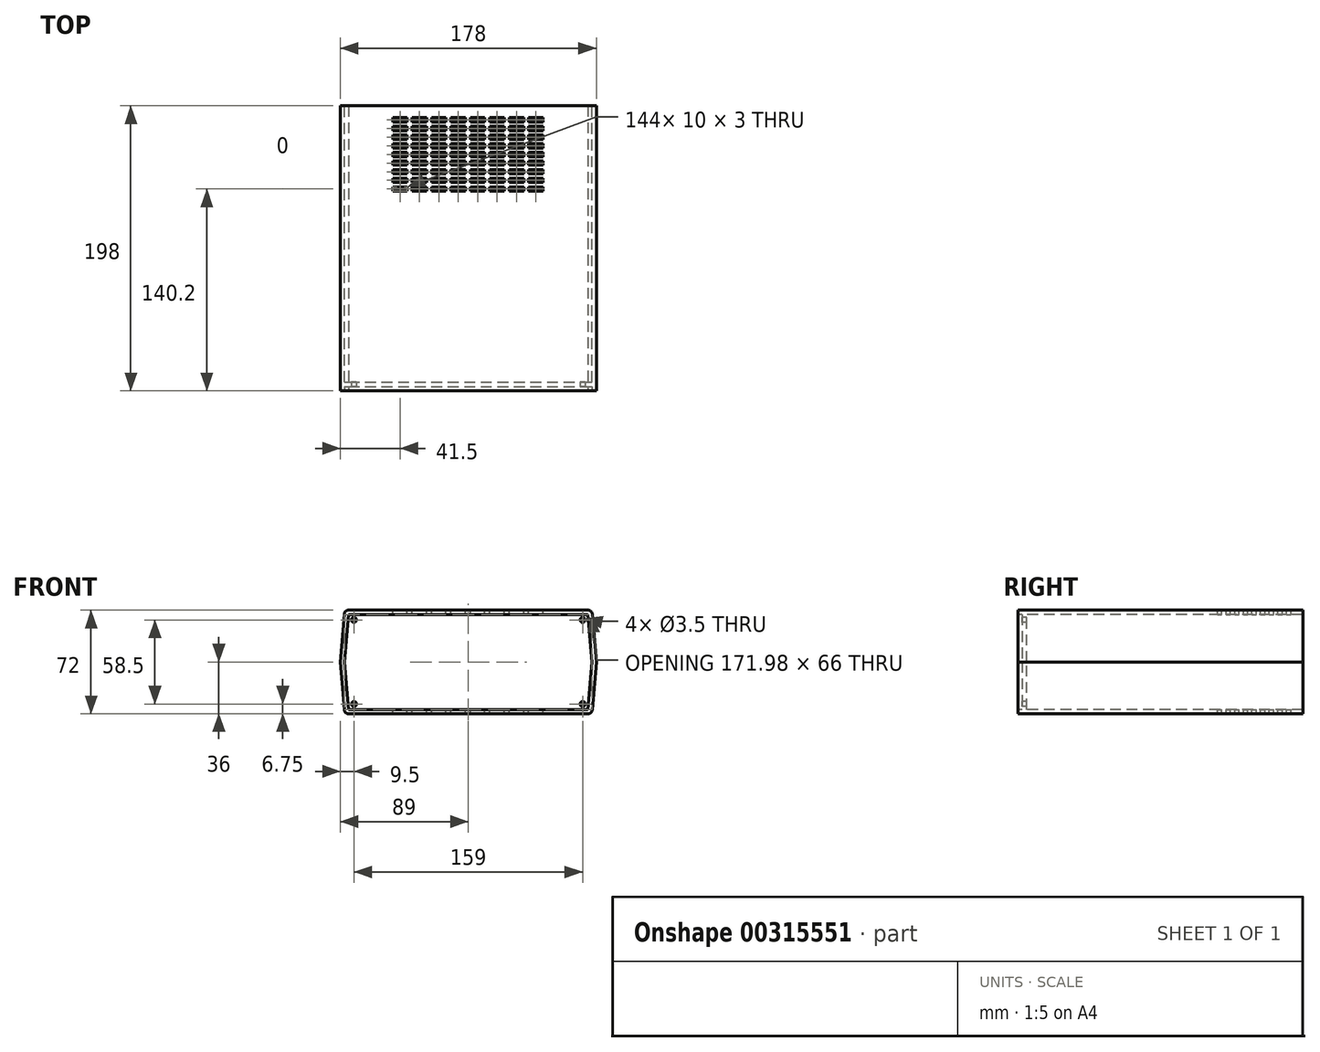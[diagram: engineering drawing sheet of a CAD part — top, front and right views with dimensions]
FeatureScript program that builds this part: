
annotation { "Feature Type Name" : "Feature", "Feature Type Description" : "" }
export const myFeature = defineFeature(function(context is Context, id is Id, definition is map)
    precondition{}
    {
        {
            var Q0;
            Q0=qCreatedBy(makeId("Front.planeOp"),FACE);
            var sketch = newSketch(context, id + "F0", { "sketchPlane" : qUnion([Q0])});
            skLineSegment(sketch, "E0", {"start": v(-89, 0) * mm, "end": v(-86, 36) * mm});
            skLineSegment(sketch, "E1", {"start": v(-86, 36) * mm, "end": v(86, 36) * mm});
            skLineSegment(sketch, "E2", {"start": v(86, 36) * mm, "end": v(89, 0) * mm});
            skLineSegment(sketch, "E3", {"start": v(-89, 0) * mm, "end": v(89, 0) * mm, "construction": true});
            skLineSegment(sketch, "E4", {"start": v(0, 0) * mm, "end": v(0, 36) * mm, "construction": true});
            skLineSegment(sketch, "E5.MirrorCS", {"start": v(86, -36) * mm, "end": v(89, 0) * mm});
            skLineSegment(sketch, "E6.MirrorCS", {"start": v(-89, 0) * mm, "end": v(-86, -36) * mm});
            skLineSegment(sketch, "E7.MirrorCS", {"start": v(-86, -36) * mm, "end": v(86, -36) * mm});
            skSolve(sketch);
        }
        {
            var Q0;
            Q0 = qSketchRegion(id + "F0", true);
            extrude(context, id + "F1", {"entities" : qUnion([Q0]), "depth" : 198 * mm});
        }
        {
            var Q0;
            Q0=makeQuery(id+"F1.opExtrude","SWEPT_EDGE",EDGE,{"disambiguationData":[OSD([sQuery(id+"F0.wireOp",EDGE,"E1"),sQuery(id+"F0.wireOp",EDGE,"E2")])]});
            var Q1;
            Q1=makeQuery(id+"F1.opExtrude","SWEPT_EDGE",EDGE,{"disambiguationData":[OSD([sQuery(id+"F0.wireOp",EDGE,"E0"),sQuery(id+"F0.wireOp",EDGE,"E1")])]});
            var Q2;
            Q2=makeQuery(id+"F1.opExtrude","SWEPT_EDGE",EDGE,{"disambiguationData":[OSD([sQuery(id+"F0.wireOp",EDGE,"E6.MirrorCS"),sQuery(id+"F0.wireOp",EDGE,"E7.MirrorCS")])]});
            var Q3;
            Q3=makeQuery(id+"F1.opExtrude","SWEPT_EDGE",EDGE,{"disambiguationData":[OSD([sQuery(id+"F0.wireOp",EDGE,"E5.MirrorCS"),sQuery(id+"F0.wireOp",EDGE,"E7.MirrorCS")])]});
            fillet(context, id + "F2", {"entities" : qUnion([Q0, Q1, Q2, Q3]), "radius" : 3 * mm, "tangentPropagation" : true, "allowEdgeOverflow" : false});
        }
        {
            var Q0;
            Q0=makeQuery(id+"F1.opExtrude","CAP_FACE",FACE,{"disambiguationData":[OSD([sQuery(id+"F0.wireOp",EDGE,"E0"),sQuery(id+"F0.wireOp",EDGE,"E1"),sQuery(id+"F0.wireOp",EDGE,"E2"),sQuery(id+"F0.wireOp",EDGE,"E5.MirrorCS"),sQuery(id+"F0.wireOp",EDGE,"E6.MirrorCS"),sQuery(id+"F0.wireOp",EDGE,"E7.MirrorCS")])],"isStart":false});
            var sketch = newSketch(context, id + "F3", { "sketchPlane" : qUnion([Q0])});
            skLineSegment(sketch, "E8.0", {"start": v(-83.24, 36) * mm, "end": v(83.24, 36) * mm, "construction": true});
            skArc(sketch, "E9.0", {"start": v(86.23, 33.25) * mm, "mid": v(85.27, 35.2) * mm, "end": v(83.24, 36) * mm, "construction": true});
            skLineSegment(sketch, "E9.1", {"start": v(86.23, 33.25) * mm, "end": v(89, 0) * mm, "construction": true});
            skLineSegment(sketch, "E10.0", {"start": v(86.23, -33.25) * mm, "end": v(89, 0) * mm, "construction": true});
            skArc(sketch, "E10.1", {"start": v(83.24, -36) * mm, "mid": v(85.27, -35.2) * mm, "end": v(86.23, -33.25) * mm, "construction": true});
            skLineSegment(sketch, "E10.2", {"start": v(-83.24, -36) * mm, "end": v(83.24, -36) * mm, "construction": true});
            skArc(sketch, "E11.0", {"start": v(-86.23, -33.25) * mm, "mid": v(-85.27, -35.2) * mm, "end": v(-83.24, -36) * mm, "construction": true});
            skLineSegment(sketch, "E11.1", {"start": v(-89, 0) * mm, "end": v(-86.23, -33.25) * mm, "construction": true});
            skLineSegment(sketch, "E12.0", {"start": v(-89, 0) * mm, "end": v(-86.23, 33.25) * mm, "construction": true});
            skArc(sketch, "E12.1", {"start": v(-83.24, 36) * mm, "mid": v(-85.27, 35.2) * mm, "end": v(-86.23, 33.25) * mm, "construction": true});
            skLineSegment(sketch, "E13.0", {"start": v(-85.99, 0) * mm, "end": v(-83.24, -33) * mm});
            skLineSegment(sketch, "E13.1", {"start": v(83.24, -33) * mm, "end": v(85.99, 0) * mm});
            skLineSegment(sketch, "E13.2", {"start": v(83.24, 33) * mm, "end": v(85.99, 0) * mm});
            skLineSegment(sketch, "E13.3", {"start": v(-83.24, -33) * mm, "end": v(83.24, -33) * mm});
            skLineSegment(sketch, "E13.4", {"start": v(-83.24, 33) * mm, "end": v(83.24, 33) * mm});
            skLineSegment(sketch, "E13.5", {"start": v(-85.99, 0) * mm, "end": v(-83.24, 33) * mm});
            skSolve(sketch);
        }
        {
            var Q0;
            Q0=makeQuery(id+"F3.imprint","IMPRINT",FACE,{"disambiguationData":[TD([[makeQuery(id+"F3.imprint","IMPRINT",EDGE,{"derivedFrom":sQuery(id+"F3.wireOp",EDGE,"E13.0")}),1.0]])]});
            extrude(context, id + "F4", {"entities" : qUnion([Q0]), "operationType" : NewBodyOperationType.REMOVE, "oppositeDirection" : true, "depth" : 3 * mm});
        }
        {
            var Q0;
            Q0=makeQuery(id+"F1.opExtrude","CAP_FACE",FACE,{"disambiguationData":[OSD([sQuery(id+"F0.wireOp",EDGE,"E0"),sQuery(id+"F0.wireOp",EDGE,"E1"),sQuery(id+"F0.wireOp",EDGE,"E2"),sQuery(id+"F0.wireOp",EDGE,"E5.MirrorCS"),sQuery(id+"F0.wireOp",EDGE,"E6.MirrorCS"),sQuery(id+"F0.wireOp",EDGE,"E7.MirrorCS")])],"isStart":true});
            shell(context, id + "F5", {"entities" : qUnion([Q0]), "thickness" : 3 * mm});
        }
        {
            var Q0;
            Q0=makeQuery(id+"F4.boolean.opBoolean","COPY",FACE,{"derivedFrom":makeQuery(id+"F4.opExtrude","CAP_FACE",FACE,{"disambiguationData":[OSD([sQuery(id+"F3.wireOp",EDGE,"E13.0"),sQuery(id+"F3.wireOp",EDGE,"E13.1"),sQuery(id+"F3.wireOp",EDGE,"E13.2"),sQuery(id+"F3.wireOp",EDGE,"E13.3"),sQuery(id+"F3.wireOp",EDGE,"E13.4"),sQuery(id+"F3.wireOp",EDGE,"E13.5")])],"isStart":false})});
            var sketch = newSketch(context, id + "F6", { "sketchPlane" : qUnion([Q0])});
            skCircle(sketch, "E14", {"center": v(-79.5, 29.25) * mm, "radius": 1.75 * mm});
            skCircle(sketch, "E15", {"center": v(79.5, 29.25) * mm, "radius": 1.75 * mm});
            skLineSegment(sketch, "E16", {"start": v(0, 0) * mm, "end": v(85.99, 0) * mm, "construction": true});
            skLineSegment(sketch, "E17", {"start": v(0, 0) * mm, "end": v(0, 33) * mm, "construction": true});
            skCircle(sketch, "E18.MirrorC", {"center": v(79.5, -29.25) * mm, "radius": 1.75 * mm});
            skCircle(sketch, "E19.MirrorC", {"center": v(-79.5, -29.25) * mm, "radius": 1.75 * mm});
            skSolve(sketch);
        }
        {
            var Q0;
            Q0 = qSketchRegion(id + "F6", true);
            extrude(context, id + "F7", {"entities" : qUnion([Q0]), "operationType" : NewBodyOperationType.REMOVE, "oppositeDirection" : true, "depth" : 25 * mm});
        }
        {
            var Q0;
            Q0=makeQuery(id+"F1.opExtrude","SWEPT_FACE",FACE,{"disambiguationData":[OSD([sQuery(id+"F0.wireOp",EDGE,"E1")])]});
            var sketch = newSketch(context, id + "F8", { "sketchPlane" : qUnion([Q0])});
            skLineSegment(sketch, "E20.bottom", {"start": v(52.5, -7) * mm, "end": v(-52.5, -7) * mm, "construction": true});
            skLineSegment(sketch, "E20.top", {"start": v(52.5, -59.3) * mm, "end": v(-52.5, -59.3) * mm, "construction": true});
            skLineSegment(sketch, "E20.left", {"start": v(52.5, -7) * mm, "end": v(52.5, -59.3) * mm, "construction": true});
            skLineSegment(sketch, "E20.right", {"start": v(-52.5, -7) * mm, "end": v(-52.5, -59.3) * mm, "construction": true});
            skPoint(sketch, "E20.middle", {"position": v(0, -33.15) * mm});
            skLineSegment(sketch, "E21.bottom", {"start": v(-52.5, -59.3) * mm, "end": v(-42.5, -59.3) * mm});
            skLineSegment(sketch, "E21.top", {"start": v(-52.5, -56.3) * mm, "end": v(-42.5, -56.3) * mm});
            skLineSegment(sketch, "E21.left", {"start": v(-52.5, -59.3) * mm, "end": v(-52.5, -56.3) * mm});
            skLineSegment(sketch, "E21.right", {"start": v(-42.5, -59.3) * mm, "end": v(-42.5, -56.3) * mm});
            skLineSegment(sketch, "E22.0.1.0", {"start": v(-52.5, -50.3) * mm, "end": v(-42.5, -50.3) * mm});
            skLineSegment(sketch, "E22.0.1.1", {"start": v(-52.5, -53.3) * mm, "end": v(-42.5, -53.3) * mm});
            skLineSegment(sketch, "E22.0.1.2", {"start": v(-52.5, -53.3) * mm, "end": v(-52.5, -50.3) * mm});
            skLineSegment(sketch, "E22.0.1.3", {"start": v(-42.5, -53.3) * mm, "end": v(-42.5, -50.3) * mm});
            skLineSegment(sketch, "E22.0.2.0", {"start": v(-52.5, -44.3) * mm, "end": v(-42.5, -44.3) * mm});
            skLineSegment(sketch, "E22.0.2.1", {"start": v(-52.5, -47.3) * mm, "end": v(-42.5, -47.3) * mm});
            skLineSegment(sketch, "E22.0.2.2", {"start": v(-52.5, -47.3) * mm, "end": v(-52.5, -44.3) * mm});
            skLineSegment(sketch, "E22.0.2.3", {"start": v(-42.5, -47.3) * mm, "end": v(-42.5, -44.3) * mm});
            skLineSegment(sketch, "E22.0.3.0", {"start": v(-52.5, -38.3) * mm, "end": v(-42.5, -38.3) * mm});
            skLineSegment(sketch, "E22.0.3.1", {"start": v(-52.5, -41.3) * mm, "end": v(-42.5, -41.3) * mm});
            skLineSegment(sketch, "E22.0.3.2", {"start": v(-52.5, -41.3) * mm, "end": v(-52.5, -38.3) * mm});
            skLineSegment(sketch, "E22.0.3.3", {"start": v(-42.5, -41.3) * mm, "end": v(-42.5, -38.3) * mm});
            skLineSegment(sketch, "E22.0.4.0", {"start": v(-52.5, -32.3) * mm, "end": v(-42.5, -32.3) * mm});
            skLineSegment(sketch, "E22.0.4.1", {"start": v(-52.5, -35.3) * mm, "end": v(-42.5, -35.3) * mm});
            skLineSegment(sketch, "E22.0.4.2", {"start": v(-52.5, -35.3) * mm, "end": v(-52.5, -32.3) * mm});
            skLineSegment(sketch, "E22.0.4.3", {"start": v(-42.5, -35.3) * mm, "end": v(-42.5, -32.3) * mm});
            skLineSegment(sketch, "E22.0.5.0", {"start": v(-52.5, -26.3) * mm, "end": v(-42.5, -26.3) * mm});
            skLineSegment(sketch, "E22.0.5.1", {"start": v(-52.5, -29.3) * mm, "end": v(-42.5, -29.3) * mm});
            skLineSegment(sketch, "E22.0.5.2", {"start": v(-52.5, -29.3) * mm, "end": v(-52.5, -26.3) * mm});
            skLineSegment(sketch, "E22.0.5.3", {"start": v(-42.5, -29.3) * mm, "end": v(-42.5, -26.3) * mm});
            skLineSegment(sketch, "E22.0.6.0", {"start": v(-52.5, -20.3) * mm, "end": v(-42.5, -20.3) * mm});
            skLineSegment(sketch, "E22.0.6.1", {"start": v(-52.5, -23.3) * mm, "end": v(-42.5, -23.3) * mm});
            skLineSegment(sketch, "E22.0.6.2", {"start": v(-52.5, -23.3) * mm, "end": v(-52.5, -20.3) * mm});
            skLineSegment(sketch, "E22.0.6.3", {"start": v(-42.5, -23.3) * mm, "end": v(-42.5, -20.3) * mm});
            skLineSegment(sketch, "E22.0.7.0", {"start": v(-52.5, -14.3) * mm, "end": v(-42.5, -14.3) * mm});
            skLineSegment(sketch, "E22.0.7.1", {"start": v(-52.5, -17.3) * mm, "end": v(-42.5, -17.3) * mm});
            skLineSegment(sketch, "E22.0.7.2", {"start": v(-52.5, -17.3) * mm, "end": v(-52.5, -14.3) * mm});
            skLineSegment(sketch, "E22.0.7.3", {"start": v(-42.5, -17.3) * mm, "end": v(-42.5, -14.3) * mm});
            skLineSegment(sketch, "E22.0.8.0", {"start": v(-52.5, -8.3) * mm, "end": v(-42.5, -8.3) * mm});
            skLineSegment(sketch, "E22.0.8.1", {"start": v(-52.5, -11.3) * mm, "end": v(-42.5, -11.3) * mm});
            skLineSegment(sketch, "E22.0.8.2", {"start": v(-52.5, -11.3) * mm, "end": v(-52.5, -8.3) * mm});
            skLineSegment(sketch, "E22.0.8.3", {"start": v(-42.5, -11.3) * mm, "end": v(-42.5, -8.3) * mm});
            skLineSegment(sketch, "E22.1.0.0", {"start": v(-39, -56.3) * mm, "end": v(-29, -56.3) * mm});
            skLineSegment(sketch, "E22.1.0.1", {"start": v(-39, -59.3) * mm, "end": v(-29, -59.3) * mm});
            skLineSegment(sketch, "E22.1.0.2", {"start": v(-39, -59.3) * mm, "end": v(-39, -56.3) * mm});
            skLineSegment(sketch, "E22.1.0.3", {"start": v(-29, -59.3) * mm, "end": v(-29, -56.3) * mm});
            skLineSegment(sketch, "E22.1.1.0", {"start": v(-39, -50.3) * mm, "end": v(-29, -50.3) * mm});
            skLineSegment(sketch, "E22.1.1.1", {"start": v(-39, -53.3) * mm, "end": v(-29, -53.3) * mm});
            skLineSegment(sketch, "E22.1.1.2", {"start": v(-39, -53.3) * mm, "end": v(-39, -50.3) * mm});
            skLineSegment(sketch, "E22.1.1.3", {"start": v(-29, -53.3) * mm, "end": v(-29, -50.3) * mm});
            skLineSegment(sketch, "E22.1.2.0", {"start": v(-39, -44.3) * mm, "end": v(-29, -44.3) * mm});
            skLineSegment(sketch, "E22.1.2.1", {"start": v(-39, -47.3) * mm, "end": v(-29, -47.3) * mm});
            skLineSegment(sketch, "E22.1.2.2", {"start": v(-39, -47.3) * mm, "end": v(-39, -44.3) * mm});
            skLineSegment(sketch, "E22.1.2.3", {"start": v(-29, -47.3) * mm, "end": v(-29, -44.3) * mm});
            skLineSegment(sketch, "E22.1.3.0", {"start": v(-39, -38.3) * mm, "end": v(-29, -38.3) * mm});
            skLineSegment(sketch, "E22.1.3.1", {"start": v(-39, -41.3) * mm, "end": v(-29, -41.3) * mm});
            skLineSegment(sketch, "E22.1.3.2", {"start": v(-39, -41.3) * mm, "end": v(-39, -38.3) * mm});
            skLineSegment(sketch, "E22.1.3.3", {"start": v(-29, -41.3) * mm, "end": v(-29, -38.3) * mm});
            skLineSegment(sketch, "E22.1.4.0", {"start": v(-39, -32.3) * mm, "end": v(-29, -32.3) * mm});
            skLineSegment(sketch, "E22.1.4.1", {"start": v(-39, -35.3) * mm, "end": v(-29, -35.3) * mm});
            skLineSegment(sketch, "E22.1.4.2", {"start": v(-39, -35.3) * mm, "end": v(-39, -32.3) * mm});
            skLineSegment(sketch, "E22.1.4.3", {"start": v(-29, -35.3) * mm, "end": v(-29, -32.3) * mm});
            skLineSegment(sketch, "E22.1.5.0", {"start": v(-39, -26.3) * mm, "end": v(-29, -26.3) * mm});
            skLineSegment(sketch, "E22.1.5.1", {"start": v(-39, -29.3) * mm, "end": v(-29, -29.3) * mm});
            skLineSegment(sketch, "E22.1.5.2", {"start": v(-39, -29.3) * mm, "end": v(-39, -26.3) * mm});
            skLineSegment(sketch, "E22.1.5.3", {"start": v(-29, -29.3) * mm, "end": v(-29, -26.3) * mm});
            skLineSegment(sketch, "E22.1.6.0", {"start": v(-39, -20.3) * mm, "end": v(-29, -20.3) * mm});
            skLineSegment(sketch, "E22.1.6.1", {"start": v(-39, -23.3) * mm, "end": v(-29, -23.3) * mm});
            skLineSegment(sketch, "E22.1.6.2", {"start": v(-39, -23.3) * mm, "end": v(-39, -20.3) * mm});
            skLineSegment(sketch, "E22.1.6.3", {"start": v(-29, -23.3) * mm, "end": v(-29, -20.3) * mm});
            skLineSegment(sketch, "E22.1.7.0", {"start": v(-39, -14.3) * mm, "end": v(-29, -14.3) * mm});
            skLineSegment(sketch, "E22.1.7.1", {"start": v(-39, -17.3) * mm, "end": v(-29, -17.3) * mm});
            skLineSegment(sketch, "E22.1.7.2", {"start": v(-39, -17.3) * mm, "end": v(-39, -14.3) * mm});
            skLineSegment(sketch, "E22.1.7.3", {"start": v(-29, -17.3) * mm, "end": v(-29, -14.3) * mm});
            skLineSegment(sketch, "E22.1.8.0", {"start": v(-39, -8.3) * mm, "end": v(-29, -8.3) * mm});
            skLineSegment(sketch, "E22.1.8.1", {"start": v(-39, -11.3) * mm, "end": v(-29, -11.3) * mm});
            skLineSegment(sketch, "E22.1.8.2", {"start": v(-39, -11.3) * mm, "end": v(-39, -8.3) * mm});
            skLineSegment(sketch, "E22.1.8.3", {"start": v(-29, -11.3) * mm, "end": v(-29, -8.3) * mm});
            skLineSegment(sketch, "E22.2.0.0", {"start": v(-25.5, -56.3) * mm, "end": v(-15.5, -56.3) * mm});
            skLineSegment(sketch, "E22.2.0.1", {"start": v(-25.5, -59.3) * mm, "end": v(-15.5, -59.3) * mm});
            skLineSegment(sketch, "E22.2.0.2", {"start": v(-25.5, -59.3) * mm, "end": v(-25.5, -56.3) * mm});
            skLineSegment(sketch, "E22.2.0.3", {"start": v(-15.5, -59.3) * mm, "end": v(-15.5, -56.3) * mm});
            skLineSegment(sketch, "E22.2.1.0", {"start": v(-25.5, -50.3) * mm, "end": v(-15.5, -50.3) * mm});
            skLineSegment(sketch, "E22.2.1.1", {"start": v(-25.5, -53.3) * mm, "end": v(-15.5, -53.3) * mm});
            skLineSegment(sketch, "E22.2.1.2", {"start": v(-25.5, -53.3) * mm, "end": v(-25.5, -50.3) * mm});
            skLineSegment(sketch, "E22.2.1.3", {"start": v(-15.5, -53.3) * mm, "end": v(-15.5, -50.3) * mm});
            skLineSegment(sketch, "E22.2.2.0", {"start": v(-25.5, -44.3) * mm, "end": v(-15.5, -44.3) * mm});
            skLineSegment(sketch, "E22.2.2.1", {"start": v(-25.5, -47.3) * mm, "end": v(-15.5, -47.3) * mm});
            skLineSegment(sketch, "E22.2.2.2", {"start": v(-25.5, -47.3) * mm, "end": v(-25.5, -44.3) * mm});
            skLineSegment(sketch, "E22.2.2.3", {"start": v(-15.5, -47.3) * mm, "end": v(-15.5, -44.3) * mm});
            skLineSegment(sketch, "E22.2.3.0", {"start": v(-25.5, -38.3) * mm, "end": v(-15.5, -38.3) * mm});
            skLineSegment(sketch, "E22.2.3.1", {"start": v(-25.5, -41.3) * mm, "end": v(-15.5, -41.3) * mm});
            skLineSegment(sketch, "E22.2.3.2", {"start": v(-25.5, -41.3) * mm, "end": v(-25.5, -38.3) * mm});
            skLineSegment(sketch, "E22.2.3.3", {"start": v(-15.5, -41.3) * mm, "end": v(-15.5, -38.3) * mm});
            skLineSegment(sketch, "E22.2.4.0", {"start": v(-25.5, -32.3) * mm, "end": v(-15.5, -32.3) * mm});
            skLineSegment(sketch, "E22.2.4.1", {"start": v(-25.5, -35.3) * mm, "end": v(-15.5, -35.3) * mm});
            skLineSegment(sketch, "E22.2.4.2", {"start": v(-25.5, -35.3) * mm, "end": v(-25.5, -32.3) * mm});
            skLineSegment(sketch, "E22.2.4.3", {"start": v(-15.5, -35.3) * mm, "end": v(-15.5, -32.3) * mm});
            skLineSegment(sketch, "E22.2.5.0", {"start": v(-25.5, -26.3) * mm, "end": v(-15.5, -26.3) * mm});
            skLineSegment(sketch, "E22.2.5.1", {"start": v(-25.5, -29.3) * mm, "end": v(-15.5, -29.3) * mm});
            skLineSegment(sketch, "E22.2.5.2", {"start": v(-25.5, -29.3) * mm, "end": v(-25.5, -26.3) * mm});
            skLineSegment(sketch, "E22.2.5.3", {"start": v(-15.5, -29.3) * mm, "end": v(-15.5, -26.3) * mm});
            skLineSegment(sketch, "E22.2.6.0", {"start": v(-25.5, -20.3) * mm, "end": v(-15.5, -20.3) * mm});
            skLineSegment(sketch, "E22.2.6.1", {"start": v(-25.5, -23.3) * mm, "end": v(-15.5, -23.3) * mm});
            skLineSegment(sketch, "E22.2.6.2", {"start": v(-25.5, -23.3) * mm, "end": v(-25.5, -20.3) * mm});
            skLineSegment(sketch, "E22.2.6.3", {"start": v(-15.5, -23.3) * mm, "end": v(-15.5, -20.3) * mm});
            skLineSegment(sketch, "E22.2.7.0", {"start": v(-25.5, -14.3) * mm, "end": v(-15.5, -14.3) * mm});
            skLineSegment(sketch, "E22.2.7.1", {"start": v(-25.5, -17.3) * mm, "end": v(-15.5, -17.3) * mm});
            skLineSegment(sketch, "E22.2.7.2", {"start": v(-25.5, -17.3) * mm, "end": v(-25.5, -14.3) * mm});
            skLineSegment(sketch, "E22.2.7.3", {"start": v(-15.5, -17.3) * mm, "end": v(-15.5, -14.3) * mm});
            skLineSegment(sketch, "E22.2.8.0", {"start": v(-25.5, -8.3) * mm, "end": v(-15.5, -8.3) * mm});
            skLineSegment(sketch, "E22.2.8.1", {"start": v(-25.5, -11.3) * mm, "end": v(-15.5, -11.3) * mm});
            skLineSegment(sketch, "E22.2.8.2", {"start": v(-25.5, -11.3) * mm, "end": v(-25.5, -8.3) * mm});
            skLineSegment(sketch, "E22.2.8.3", {"start": v(-15.5, -11.3) * mm, "end": v(-15.5, -8.3) * mm});
            skLineSegment(sketch, "E22.3.0.0", {"start": v(-12, -56.3) * mm, "end": v(-2, -56.3) * mm});
            skLineSegment(sketch, "E22.3.0.1", {"start": v(-12, -59.3) * mm, "end": v(-2, -59.3) * mm});
            skLineSegment(sketch, "E22.3.0.2", {"start": v(-12, -59.3) * mm, "end": v(-12, -56.3) * mm});
            skLineSegment(sketch, "E22.3.0.3", {"start": v(-2, -59.3) * mm, "end": v(-2, -56.3) * mm});
            skLineSegment(sketch, "E22.3.1.0", {"start": v(-12, -50.3) * mm, "end": v(-2, -50.3) * mm});
            skLineSegment(sketch, "E22.3.1.1", {"start": v(-12, -53.3) * mm, "end": v(-2, -53.3) * mm});
            skLineSegment(sketch, "E22.3.1.2", {"start": v(-12, -53.3) * mm, "end": v(-12, -50.3) * mm});
            skLineSegment(sketch, "E22.3.1.3", {"start": v(-2, -53.3) * mm, "end": v(-2, -50.3) * mm});
            skLineSegment(sketch, "E22.3.2.0", {"start": v(-12, -44.3) * mm, "end": v(-2, -44.3) * mm});
            skLineSegment(sketch, "E22.3.2.1", {"start": v(-12, -47.3) * mm, "end": v(-2, -47.3) * mm});
            skLineSegment(sketch, "E22.3.2.2", {"start": v(-12, -47.3) * mm, "end": v(-12, -44.3) * mm});
            skLineSegment(sketch, "E22.3.2.3", {"start": v(-2, -47.3) * mm, "end": v(-2, -44.3) * mm});
            skLineSegment(sketch, "E22.3.3.0", {"start": v(-12, -38.3) * mm, "end": v(-2, -38.3) * mm});
            skLineSegment(sketch, "E22.3.3.1", {"start": v(-12, -41.3) * mm, "end": v(-2, -41.3) * mm});
            skLineSegment(sketch, "E22.3.3.2", {"start": v(-12, -41.3) * mm, "end": v(-12, -38.3) * mm});
            skLineSegment(sketch, "E22.3.3.3", {"start": v(-2, -41.3) * mm, "end": v(-2, -38.3) * mm});
            skLineSegment(sketch, "E22.3.4.0", {"start": v(-12, -32.3) * mm, "end": v(-2, -32.3) * mm});
            skLineSegment(sketch, "E22.3.4.1", {"start": v(-12, -35.3) * mm, "end": v(-2, -35.3) * mm});
            skLineSegment(sketch, "E22.3.4.2", {"start": v(-12, -35.3) * mm, "end": v(-12, -32.3) * mm});
            skLineSegment(sketch, "E22.3.4.3", {"start": v(-2, -35.3) * mm, "end": v(-2, -32.3) * mm});
            skLineSegment(sketch, "E22.3.5.0", {"start": v(-12, -26.3) * mm, "end": v(-2, -26.3) * mm});
            skLineSegment(sketch, "E22.3.5.1", {"start": v(-12, -29.3) * mm, "end": v(-2, -29.3) * mm});
            skLineSegment(sketch, "E22.3.5.2", {"start": v(-12, -29.3) * mm, "end": v(-12, -26.3) * mm});
            skLineSegment(sketch, "E22.3.5.3", {"start": v(-2, -29.3) * mm, "end": v(-2, -26.3) * mm});
            skLineSegment(sketch, "E22.3.6.0", {"start": v(-12, -20.3) * mm, "end": v(-2, -20.3) * mm});
            skLineSegment(sketch, "E22.3.6.1", {"start": v(-12, -23.3) * mm, "end": v(-2, -23.3) * mm});
            skLineSegment(sketch, "E22.3.6.2", {"start": v(-12, -23.3) * mm, "end": v(-12, -20.3) * mm});
            skLineSegment(sketch, "E22.3.6.3", {"start": v(-2, -23.3) * mm, "end": v(-2, -20.3) * mm});
            skLineSegment(sketch, "E22.3.7.0", {"start": v(-12, -14.3) * mm, "end": v(-2, -14.3) * mm});
            skLineSegment(sketch, "E22.3.7.1", {"start": v(-12, -17.3) * mm, "end": v(-2, -17.3) * mm});
            skLineSegment(sketch, "E22.3.7.2", {"start": v(-12, -17.3) * mm, "end": v(-12, -14.3) * mm});
            skLineSegment(sketch, "E22.3.7.3", {"start": v(-2, -17.3) * mm, "end": v(-2, -14.3) * mm});
            skLineSegment(sketch, "E22.3.8.0", {"start": v(-12, -8.3) * mm, "end": v(-2, -8.3) * mm});
            skLineSegment(sketch, "E22.3.8.1", {"start": v(-12, -11.3) * mm, "end": v(-2, -11.3) * mm});
            skLineSegment(sketch, "E22.3.8.2", {"start": v(-12, -11.3) * mm, "end": v(-12, -8.3) * mm});
            skLineSegment(sketch, "E22.3.8.3", {"start": v(-2, -11.3) * mm, "end": v(-2, -8.3) * mm});
            skLineSegment(sketch, "E22.4.0.0", {"start": v(1.5, -56.3) * mm, "end": v(11.5, -56.3) * mm});
            skLineSegment(sketch, "E22.4.0.1", {"start": v(1.5, -59.3) * mm, "end": v(11.5, -59.3) * mm});
            skLineSegment(sketch, "E22.4.0.2", {"start": v(1.5, -59.3) * mm, "end": v(1.5, -56.3) * mm});
            skLineSegment(sketch, "E22.4.0.3", {"start": v(11.5, -59.3) * mm, "end": v(11.5, -56.3) * mm});
            skLineSegment(sketch, "E22.4.1.0", {"start": v(1.5, -50.3) * mm, "end": v(11.5, -50.3) * mm});
            skLineSegment(sketch, "E22.4.1.1", {"start": v(1.5, -53.3) * mm, "end": v(11.5, -53.3) * mm});
            skLineSegment(sketch, "E22.4.1.2", {"start": v(1.5, -53.3) * mm, "end": v(1.5, -50.3) * mm});
            skLineSegment(sketch, "E22.4.1.3", {"start": v(11.5, -53.3) * mm, "end": v(11.5, -50.3) * mm});
            skLineSegment(sketch, "E22.4.2.0", {"start": v(1.5, -44.3) * mm, "end": v(11.5, -44.3) * mm});
            skLineSegment(sketch, "E22.4.2.1", {"start": v(1.5, -47.3) * mm, "end": v(11.5, -47.3) * mm});
            skLineSegment(sketch, "E22.4.2.2", {"start": v(1.5, -47.3) * mm, "end": v(1.5, -44.3) * mm});
            skLineSegment(sketch, "E22.4.2.3", {"start": v(11.5, -47.3) * mm, "end": v(11.5, -44.3) * mm});
            skLineSegment(sketch, "E22.4.3.0", {"start": v(1.5, -38.3) * mm, "end": v(11.5, -38.3) * mm});
            skLineSegment(sketch, "E22.4.3.1", {"start": v(1.5, -41.3) * mm, "end": v(11.5, -41.3) * mm});
            skLineSegment(sketch, "E22.4.3.2", {"start": v(1.5, -41.3) * mm, "end": v(1.5, -38.3) * mm});
            skLineSegment(sketch, "E22.4.3.3", {"start": v(11.5, -41.3) * mm, "end": v(11.5, -38.3) * mm});
            skLineSegment(sketch, "E22.4.4.0", {"start": v(1.5, -32.3) * mm, "end": v(11.5, -32.3) * mm});
            skLineSegment(sketch, "E22.4.4.1", {"start": v(1.5, -35.3) * mm, "end": v(11.5, -35.3) * mm});
            skLineSegment(sketch, "E22.4.4.2", {"start": v(1.5, -35.3) * mm, "end": v(1.5, -32.3) * mm});
            skLineSegment(sketch, "E22.4.4.3", {"start": v(11.5, -35.3) * mm, "end": v(11.5, -32.3) * mm});
            skLineSegment(sketch, "E22.4.5.0", {"start": v(1.5, -26.3) * mm, "end": v(11.5, -26.3) * mm});
            skLineSegment(sketch, "E22.4.5.1", {"start": v(1.5, -29.3) * mm, "end": v(11.5, -29.3) * mm});
            skLineSegment(sketch, "E22.4.5.2", {"start": v(1.5, -29.3) * mm, "end": v(1.5, -26.3) * mm});
            skLineSegment(sketch, "E22.4.5.3", {"start": v(11.5, -29.3) * mm, "end": v(11.5, -26.3) * mm});
            skLineSegment(sketch, "E22.4.6.0", {"start": v(1.5, -20.3) * mm, "end": v(11.5, -20.3) * mm});
            skLineSegment(sketch, "E22.4.6.1", {"start": v(1.5, -23.3) * mm, "end": v(11.5, -23.3) * mm});
            skLineSegment(sketch, "E22.4.6.2", {"start": v(1.5, -23.3) * mm, "end": v(1.5, -20.3) * mm});
            skLineSegment(sketch, "E22.4.6.3", {"start": v(11.5, -23.3) * mm, "end": v(11.5, -20.3) * mm});
            skLineSegment(sketch, "E22.4.7.0", {"start": v(1.5, -14.3) * mm, "end": v(11.5, -14.3) * mm});
            skLineSegment(sketch, "E22.4.7.1", {"start": v(1.5, -17.3) * mm, "end": v(11.5, -17.3) * mm});
            skLineSegment(sketch, "E22.4.7.2", {"start": v(1.5, -17.3) * mm, "end": v(1.5, -14.3) * mm});
            skLineSegment(sketch, "E22.4.7.3", {"start": v(11.5, -17.3) * mm, "end": v(11.5, -14.3) * mm});
            skLineSegment(sketch, "E22.4.8.0", {"start": v(1.5, -8.3) * mm, "end": v(11.5, -8.3) * mm});
            skLineSegment(sketch, "E22.4.8.1", {"start": v(1.5, -11.3) * mm, "end": v(11.5, -11.3) * mm});
            skLineSegment(sketch, "E22.4.8.2", {"start": v(1.5, -11.3) * mm, "end": v(1.5, -8.3) * mm});
            skLineSegment(sketch, "E22.4.8.3", {"start": v(11.5, -11.3) * mm, "end": v(11.5, -8.3) * mm});
            skLineSegment(sketch, "E22.5.0.0", {"start": v(15, -56.3) * mm, "end": v(25, -56.3) * mm});
            skLineSegment(sketch, "E22.5.0.1", {"start": v(15, -59.3) * mm, "end": v(25, -59.3) * mm});
            skLineSegment(sketch, "E22.5.0.2", {"start": v(15, -59.3) * mm, "end": v(15, -56.3) * mm});
            skLineSegment(sketch, "E22.5.0.3", {"start": v(25, -59.3) * mm, "end": v(25, -56.3) * mm});
            skLineSegment(sketch, "E22.5.1.0", {"start": v(15, -50.3) * mm, "end": v(25, -50.3) * mm});
            skLineSegment(sketch, "E22.5.1.1", {"start": v(15, -53.3) * mm, "end": v(25, -53.3) * mm});
            skLineSegment(sketch, "E22.5.1.2", {"start": v(15, -53.3) * mm, "end": v(15, -50.3) * mm});
            skLineSegment(sketch, "E22.5.1.3", {"start": v(25, -53.3) * mm, "end": v(25, -50.3) * mm});
            skLineSegment(sketch, "E22.5.2.0", {"start": v(15, -44.3) * mm, "end": v(25, -44.3) * mm});
            skLineSegment(sketch, "E22.5.2.1", {"start": v(15, -47.3) * mm, "end": v(25, -47.3) * mm});
            skLineSegment(sketch, "E22.5.2.2", {"start": v(15, -47.3) * mm, "end": v(15, -44.3) * mm});
            skLineSegment(sketch, "E22.5.2.3", {"start": v(25, -47.3) * mm, "end": v(25, -44.3) * mm});
            skLineSegment(sketch, "E22.5.3.0", {"start": v(15, -38.3) * mm, "end": v(25, -38.3) * mm});
            skLineSegment(sketch, "E22.5.3.1", {"start": v(15, -41.3) * mm, "end": v(25, -41.3) * mm});
            skLineSegment(sketch, "E22.5.3.2", {"start": v(15, -41.3) * mm, "end": v(15, -38.3) * mm});
            skLineSegment(sketch, "E22.5.3.3", {"start": v(25, -41.3) * mm, "end": v(25, -38.3) * mm});
            skLineSegment(sketch, "E22.5.4.0", {"start": v(15, -32.3) * mm, "end": v(25, -32.3) * mm});
            skLineSegment(sketch, "E22.5.4.1", {"start": v(15, -35.3) * mm, "end": v(25, -35.3) * mm});
            skLineSegment(sketch, "E22.5.4.2", {"start": v(15, -35.3) * mm, "end": v(15, -32.3) * mm});
            skLineSegment(sketch, "E22.5.4.3", {"start": v(25, -35.3) * mm, "end": v(25, -32.3) * mm});
            skLineSegment(sketch, "E22.5.5.0", {"start": v(15, -26.3) * mm, "end": v(25, -26.3) * mm});
            skLineSegment(sketch, "E22.5.5.1", {"start": v(15, -29.3) * mm, "end": v(25, -29.3) * mm});
            skLineSegment(sketch, "E22.5.5.2", {"start": v(15, -29.3) * mm, "end": v(15, -26.3) * mm});
            skLineSegment(sketch, "E22.5.5.3", {"start": v(25, -29.3) * mm, "end": v(25, -26.3) * mm});
            skLineSegment(sketch, "E22.5.6.0", {"start": v(15, -20.3) * mm, "end": v(25, -20.3) * mm});
            skLineSegment(sketch, "E22.5.6.1", {"start": v(15, -23.3) * mm, "end": v(25, -23.3) * mm});
            skLineSegment(sketch, "E22.5.6.2", {"start": v(15, -23.3) * mm, "end": v(15, -20.3) * mm});
            skLineSegment(sketch, "E22.5.6.3", {"start": v(25, -23.3) * mm, "end": v(25, -20.3) * mm});
            skLineSegment(sketch, "E22.5.7.0", {"start": v(15, -14.3) * mm, "end": v(25, -14.3) * mm});
            skLineSegment(sketch, "E22.5.7.1", {"start": v(15, -17.3) * mm, "end": v(25, -17.3) * mm});
            skLineSegment(sketch, "E22.5.7.2", {"start": v(15, -17.3) * mm, "end": v(15, -14.3) * mm});
            skLineSegment(sketch, "E22.5.7.3", {"start": v(25, -17.3) * mm, "end": v(25, -14.3) * mm});
            skLineSegment(sketch, "E22.5.8.0", {"start": v(15, -8.3) * mm, "end": v(25, -8.3) * mm});
            skLineSegment(sketch, "E22.5.8.1", {"start": v(15, -11.3) * mm, "end": v(25, -11.3) * mm});
            skLineSegment(sketch, "E22.5.8.2", {"start": v(15, -11.3) * mm, "end": v(15, -8.3) * mm});
            skLineSegment(sketch, "E22.5.8.3", {"start": v(25, -11.3) * mm, "end": v(25, -8.3) * mm});
            skLineSegment(sketch, "E22.6.0.0", {"start": v(28.5, -56.3) * mm, "end": v(38.5, -56.3) * mm});
            skLineSegment(sketch, "E22.6.0.1", {"start": v(28.5, -59.3) * mm, "end": v(38.5, -59.3) * mm});
            skLineSegment(sketch, "E22.6.0.2", {"start": v(28.5, -59.3) * mm, "end": v(28.5, -56.3) * mm});
            skLineSegment(sketch, "E22.6.0.3", {"start": v(38.5, -59.3) * mm, "end": v(38.5, -56.3) * mm});
            skLineSegment(sketch, "E22.6.1.0", {"start": v(28.5, -50.3) * mm, "end": v(38.5, -50.3) * mm});
            skLineSegment(sketch, "E22.6.1.1", {"start": v(28.5, -53.3) * mm, "end": v(38.5, -53.3) * mm});
            skLineSegment(sketch, "E22.6.1.2", {"start": v(28.5, -53.3) * mm, "end": v(28.5, -50.3) * mm});
            skLineSegment(sketch, "E22.6.1.3", {"start": v(38.5, -53.3) * mm, "end": v(38.5, -50.3) * mm});
            skLineSegment(sketch, "E22.6.2.0", {"start": v(28.5, -44.3) * mm, "end": v(38.5, -44.3) * mm});
            skLineSegment(sketch, "E22.6.2.1", {"start": v(28.5, -47.3) * mm, "end": v(38.5, -47.3) * mm});
            skLineSegment(sketch, "E22.6.2.2", {"start": v(28.5, -47.3) * mm, "end": v(28.5, -44.3) * mm});
            skLineSegment(sketch, "E22.6.2.3", {"start": v(38.5, -47.3) * mm, "end": v(38.5, -44.3) * mm});
            skLineSegment(sketch, "E22.6.3.0", {"start": v(28.5, -38.3) * mm, "end": v(38.5, -38.3) * mm});
            skLineSegment(sketch, "E22.6.3.1", {"start": v(28.5, -41.3) * mm, "end": v(38.5, -41.3) * mm});
            skLineSegment(sketch, "E22.6.3.2", {"start": v(28.5, -41.3) * mm, "end": v(28.5, -38.3) * mm});
            skLineSegment(sketch, "E22.6.3.3", {"start": v(38.5, -41.3) * mm, "end": v(38.5, -38.3) * mm});
            skLineSegment(sketch, "E22.6.4.0", {"start": v(28.5, -32.3) * mm, "end": v(38.5, -32.3) * mm});
            skLineSegment(sketch, "E22.6.4.1", {"start": v(28.5, -35.3) * mm, "end": v(38.5, -35.3) * mm});
            skLineSegment(sketch, "E22.6.4.2", {"start": v(28.5, -35.3) * mm, "end": v(28.5, -32.3) * mm});
            skLineSegment(sketch, "E22.6.4.3", {"start": v(38.5, -35.3) * mm, "end": v(38.5, -32.3) * mm});
            skLineSegment(sketch, "E22.6.5.0", {"start": v(28.5, -26.3) * mm, "end": v(38.5, -26.3) * mm});
            skLineSegment(sketch, "E22.6.5.1", {"start": v(28.5, -29.3) * mm, "end": v(38.5, -29.3) * mm});
            skLineSegment(sketch, "E22.6.5.2", {"start": v(28.5, -29.3) * mm, "end": v(28.5, -26.3) * mm});
            skLineSegment(sketch, "E22.6.5.3", {"start": v(38.5, -29.3) * mm, "end": v(38.5, -26.3) * mm});
            skLineSegment(sketch, "E22.6.6.0", {"start": v(28.5, -20.3) * mm, "end": v(38.5, -20.3) * mm});
            skLineSegment(sketch, "E22.6.6.1", {"start": v(28.5, -23.3) * mm, "end": v(38.5, -23.3) * mm});
            skLineSegment(sketch, "E22.6.6.2", {"start": v(28.5, -23.3) * mm, "end": v(28.5, -20.3) * mm});
            skLineSegment(sketch, "E22.6.6.3", {"start": v(38.5, -23.3) * mm, "end": v(38.5, -20.3) * mm});
            skLineSegment(sketch, "E22.6.7.0", {"start": v(28.5, -14.3) * mm, "end": v(38.5, -14.3) * mm});
            skLineSegment(sketch, "E22.6.7.1", {"start": v(28.5, -17.3) * mm, "end": v(38.5, -17.3) * mm});
            skLineSegment(sketch, "E22.6.7.2", {"start": v(28.5, -17.3) * mm, "end": v(28.5, -14.3) * mm});
            skLineSegment(sketch, "E22.6.7.3", {"start": v(38.5, -17.3) * mm, "end": v(38.5, -14.3) * mm});
            skLineSegment(sketch, "E22.6.8.0", {"start": v(28.5, -8.3) * mm, "end": v(38.5, -8.3) * mm});
            skLineSegment(sketch, "E22.6.8.1", {"start": v(28.5, -11.3) * mm, "end": v(38.5, -11.3) * mm});
            skLineSegment(sketch, "E22.6.8.2", {"start": v(28.5, -11.3) * mm, "end": v(28.5, -8.3) * mm});
            skLineSegment(sketch, "E22.6.8.3", {"start": v(38.5, -11.3) * mm, "end": v(38.5, -8.3) * mm});
            skLineSegment(sketch, "E22.7.0.0", {"start": v(42, -56.3) * mm, "end": v(52, -56.3) * mm});
            skLineSegment(sketch, "E22.7.0.1", {"start": v(42, -59.3) * mm, "end": v(52, -59.3) * mm});
            skLineSegment(sketch, "E22.7.0.2", {"start": v(42, -59.3) * mm, "end": v(42, -56.3) * mm});
            skLineSegment(sketch, "E22.7.0.3", {"start": v(52, -59.3) * mm, "end": v(52, -56.3) * mm});
            skLineSegment(sketch, "E22.7.1.0", {"start": v(42, -50.3) * mm, "end": v(52, -50.3) * mm});
            skLineSegment(sketch, "E22.7.1.1", {"start": v(42, -53.3) * mm, "end": v(52, -53.3) * mm});
            skLineSegment(sketch, "E22.7.1.2", {"start": v(42, -53.3) * mm, "end": v(42, -50.3) * mm});
            skLineSegment(sketch, "E22.7.1.3", {"start": v(52, -53.3) * mm, "end": v(52, -50.3) * mm});
            skLineSegment(sketch, "E22.7.2.0", {"start": v(42, -44.3) * mm, "end": v(52, -44.3) * mm});
            skLineSegment(sketch, "E22.7.2.1", {"start": v(42, -47.3) * mm, "end": v(52, -47.3) * mm});
            skLineSegment(sketch, "E22.7.2.2", {"start": v(42, -47.3) * mm, "end": v(42, -44.3) * mm});
            skLineSegment(sketch, "E22.7.2.3", {"start": v(52, -47.3) * mm, "end": v(52, -44.3) * mm});
            skLineSegment(sketch, "E22.7.3.0", {"start": v(42, -38.3) * mm, "end": v(52, -38.3) * mm});
            skLineSegment(sketch, "E22.7.3.1", {"start": v(42, -41.3) * mm, "end": v(52, -41.3) * mm});
            skLineSegment(sketch, "E22.7.3.2", {"start": v(42, -41.3) * mm, "end": v(42, -38.3) * mm});
            skLineSegment(sketch, "E22.7.3.3", {"start": v(52, -41.3) * mm, "end": v(52, -38.3) * mm});
            skLineSegment(sketch, "E22.7.4.0", {"start": v(42, -32.3) * mm, "end": v(52, -32.3) * mm});
            skLineSegment(sketch, "E22.7.4.1", {"start": v(42, -35.3) * mm, "end": v(52, -35.3) * mm});
            skLineSegment(sketch, "E22.7.4.2", {"start": v(42, -35.3) * mm, "end": v(42, -32.3) * mm});
            skLineSegment(sketch, "E22.7.4.3", {"start": v(52, -35.3) * mm, "end": v(52, -32.3) * mm});
            skLineSegment(sketch, "E22.7.5.0", {"start": v(42, -26.3) * mm, "end": v(52, -26.3) * mm});
            skLineSegment(sketch, "E22.7.5.1", {"start": v(42, -29.3) * mm, "end": v(52, -29.3) * mm});
            skLineSegment(sketch, "E22.7.5.2", {"start": v(42, -29.3) * mm, "end": v(42, -26.3) * mm});
            skLineSegment(sketch, "E22.7.5.3", {"start": v(52, -29.3) * mm, "end": v(52, -26.3) * mm});
            skLineSegment(sketch, "E22.7.6.0", {"start": v(42, -20.3) * mm, "end": v(52, -20.3) * mm});
            skLineSegment(sketch, "E22.7.6.1", {"start": v(42, -23.3) * mm, "end": v(52, -23.3) * mm});
            skLineSegment(sketch, "E22.7.6.2", {"start": v(42, -23.3) * mm, "end": v(42, -20.3) * mm});
            skLineSegment(sketch, "E22.7.6.3", {"start": v(52, -23.3) * mm, "end": v(52, -20.3) * mm});
            skLineSegment(sketch, "E22.7.7.0", {"start": v(42, -14.3) * mm, "end": v(52, -14.3) * mm});
            skLineSegment(sketch, "E22.7.7.1", {"start": v(42, -17.3) * mm, "end": v(52, -17.3) * mm});
            skLineSegment(sketch, "E22.7.7.2", {"start": v(42, -17.3) * mm, "end": v(42, -14.3) * mm});
            skLineSegment(sketch, "E22.7.7.3", {"start": v(52, -17.3) * mm, "end": v(52, -14.3) * mm});
            skLineSegment(sketch, "E22.7.8.0", {"start": v(42, -8.3) * mm, "end": v(52, -8.3) * mm});
            skLineSegment(sketch, "E22.7.8.1", {"start": v(42, -11.3) * mm, "end": v(52, -11.3) * mm});
            skLineSegment(sketch, "E22.7.8.2", {"start": v(42, -11.3) * mm, "end": v(42, -8.3) * mm});
            skLineSegment(sketch, "E22.7.8.3", {"start": v(52, -11.3) * mm, "end": v(52, -8.3) * mm});
            skLineSegment(sketch, "E22.direction1", {"start": v(-52.5, -59.3) * mm, "end": v(-39, -59.3) * mm, "construction": true});
            skLineSegment(sketch, "E22.direction2", {"start": v(-52.5, -59.3) * mm, "end": v(-52.5, -53.3) * mm, "construction": true});
            skSolve(sketch);
        }
        {
            var Q0;
            Q0 = qSketchRegion(id + "F8", true);
            extrude(context, id + "F9", {"entities" : qUnion([Q0]), "operationType" : NewBodyOperationType.REMOVE, "endBound" : BoundingType.THROUGH_ALL, "oppositeDirection" : true, "depth" : 25 * mm});
        }
    });
